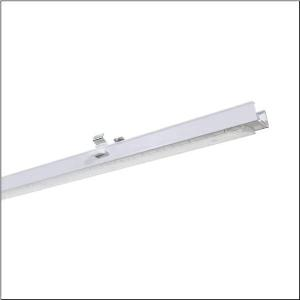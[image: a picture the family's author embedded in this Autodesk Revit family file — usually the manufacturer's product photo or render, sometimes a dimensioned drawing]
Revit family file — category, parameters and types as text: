
# Revit family: trunking_flex_31_51re12ma46b
name_source: partatom
category: Lighting Fixtures
units: mm (PartAtom-declared; Revit-internal decimal feet)

## family parameters
Cut with Voids When Loaded = No
Host = Face
Light Source = No
Part Type = Normal
Room Calculation Point = No
Round Connector Dimension = Use Diameter
Shared = No

## types (1)
- --- (1 x LED, 6400 lm, 40 W, 4000K)
    Apparent Load = 40 VA
    CIE Flux Codes = 65 91 98 99 100
    Color Rendering = 80
    Color Temperature = 4000K
    Default Elevation = 1800 mm
    Description = Trunking Flex 31, luminaire insert, of extruded aluminium section, coated, traffic white (RAL 9016), length: 1.172mm, width: 91mm, height: 53mm, LED rated luminous flux: 6.400lm, light colour: 840, control gear: ON/OFF Multilumen, with system connector: socket, mains connection: 220..240V, AC, 50/60Hz, rated input power: 40W, luminous flux adjustable on luminaire in four steps (3420/4540/5580/6630lm), connected load according to luminous flux setting (20/26/33/40W), primary light control with lens, of plastic, primary optical cover: cover, of PMMA, light emission: direct distribution, protection rating (complete): IP20, insulation class (complete): insulation class I (protective earthing), certification: CE, UKCA, impact resistance: IK02, permissible ambient temperature for indoor applications: -20..+40°C, packaging unit: 1 piece
    Height = 58 mm
    Lamp = 1 x LED
    Lamp Light Flux = 6400 lm
    Lamp Power = 40 W
    Lamp count = 1
    Length = 1172 mm
    Luminous efficacy = 160 lm/W
    Manufacturer = Siteco
    ModVariant = No
    Model = 51RE12MA46B
    Mounting Place = Ceiling
    Mounting Type = Pendant
    Number of Poles = 1
    OnlyDefault = Yes
    Power Factor = 1
    Product Name = Trunking Flex 31
    Product group = luminaire insert
    ProductGroupID = 901
    Protection Class = Protection class I
    Protection Degree = IP 20
    RLX_Detail_Level = 1
    RLX_Emergency_Light_Flux = 0 lm
    RLX_Emergency_Type = 0
    RLX_Emergency_Type_DB = No
    RlxData = <blob elided: 19929 chars, md5=913b4c15>
    Socket = socket
    Standby Power = 0 W
    System Light Flux = 6400 lm
    System Power = 40 W
    Type Comments = factory setting: luminous flux: 100 % | (ON | ON) | 300 mA
    Type Image = l_1266702.jpg
    URL = http://relux.com
    VarID = @adj_018681
    Voltage = 0 V
    Weight = 0.00 kg
    Width = 65 mm

## geometry (parser evidence)
native form markers: Blend x4, Sweep x11
no freeform markers — native parametric forms only
